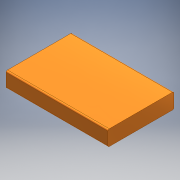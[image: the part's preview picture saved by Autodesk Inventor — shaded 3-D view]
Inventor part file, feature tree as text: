
AUTODESK INVENTOR PART (.ipt)
format: ipt  version: 2016 (Build 200138000, 138)  size: 110,080 bytes
history: native  units: mm
features: extrude x1, fillet x1, sketch x1
ambient origin geometry x8: Origin, YZ Plane, XZ Plane, XY Plane, X Axis, Y Axis, Z Axis, Center Point
bodies: Solid1 (feature_tree)
feature tree (3):
  extrude  "Extrusion1"  Depth=37.0mm
  fillet  "Fillet1"  Radius=5.6mm
  sketch  "Sketch1"  dims[d0=24.0mm d1=37.0mm d2=5.6mm d3=0.0mm d4=0.5mm]
